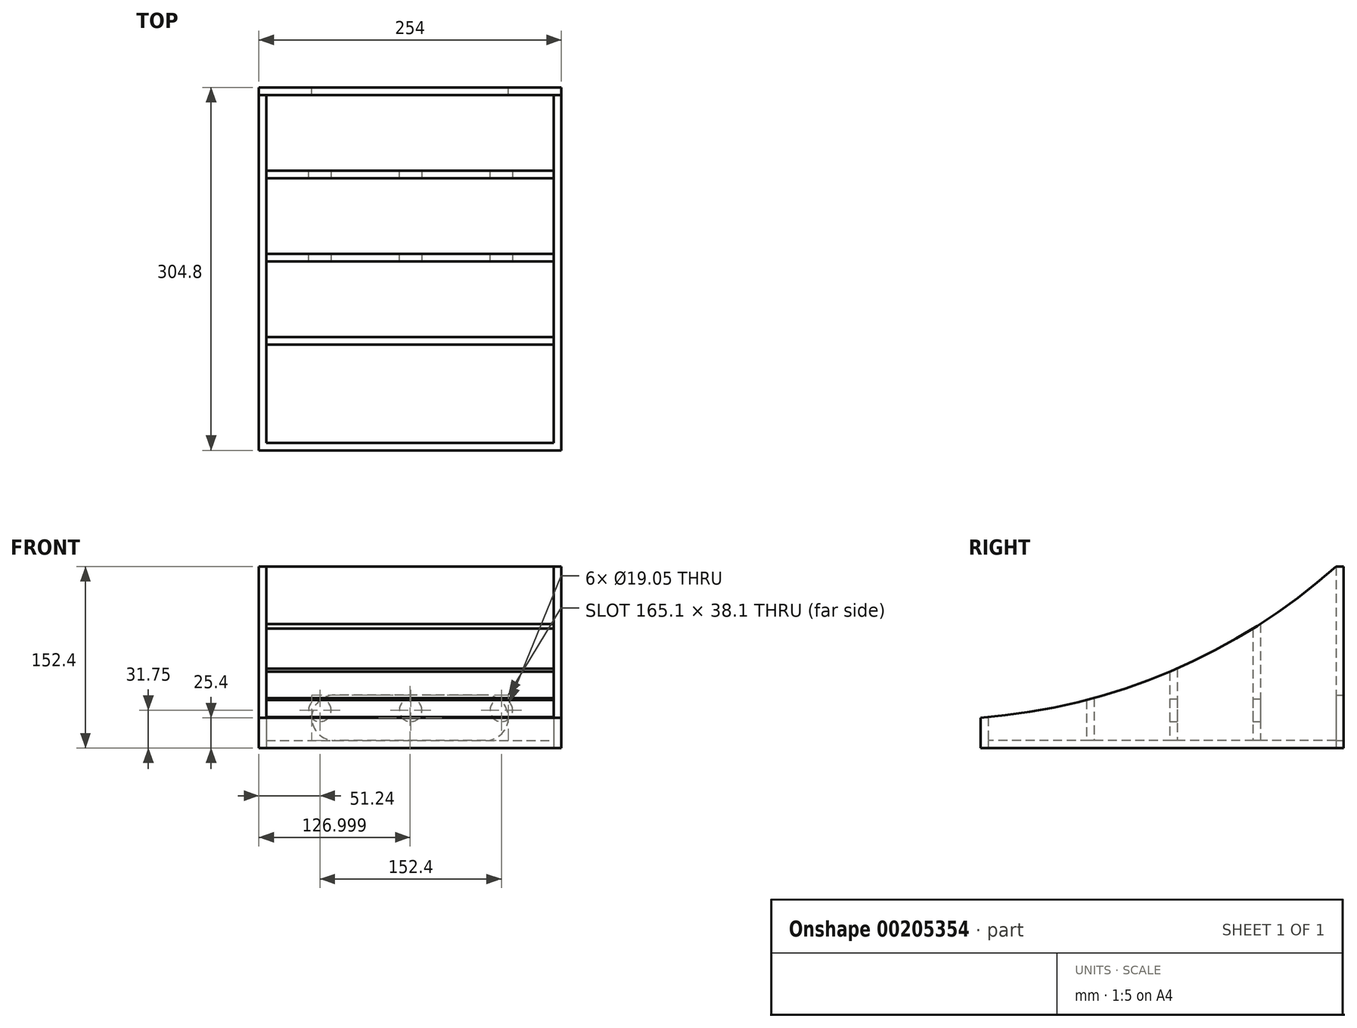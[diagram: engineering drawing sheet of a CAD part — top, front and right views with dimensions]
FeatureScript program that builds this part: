
annotation { "Feature Type Name" : "Feature", "Feature Type Description" : "" }
export const myFeature = defineFeature(function(context is Context, id is Id, definition is map)
    precondition{}
    {
        {
            var Q0;
            Q0=qCreatedBy(makeId("Top.planeOp"),FACE);
            var sketch = newSketch(context, id + "F0", { "sketchPlane" : qUnion([Q0])});
            skLineSegment(sketch, "E0.bottom", {"start": v(-127.44, 180.43) * mm, "end": v(126.56, 180.43) * mm});
            skLineSegment(sketch, "E0.top", {"start": v(-127.44, -124.37) * mm, "end": v(126.56, -124.37) * mm});
            skLineSegment(sketch, "E0.left", {"start": v(-127.44, 180.43) * mm, "end": v(-127.44, -124.37) * mm});
            skLineSegment(sketch, "E0.right", {"start": v(126.56, 180.43) * mm, "end": v(126.56, -124.37) * mm});
            skLineSegment(sketch, "E1.0", {"start": v(-121.1, 174.08) * mm, "end": v(120.2, 174.08) * mm});
            skLineSegment(sketch, "E1.1", {"start": v(-121.1, 174.08) * mm, "end": v(-121.1, -118.02) * mm});
            skLineSegment(sketch, "E1.2", {"start": v(-121.1, -118.02) * mm, "end": v(120.2, -118.02) * mm});
            skLineSegment(sketch, "E1.3", {"start": v(120.2, 174.08) * mm, "end": v(120.2, -118.02) * mm});
            skSolve(sketch);
        }
        {
            var Q0;
            Q0=makeQuery(id+"F0.imprint","IMPRINT",FACE,{"disambiguationData":[TD([[makeQuery(id+"F0.imprint","IMPRINT",EDGE,{"derivedFrom":sQuery(id+"F0.wireOp",EDGE,"E0.bottom")}),-1.0]])]});
            extrude(context, id + "F1", {"entities" : qUnion([Q0]), "depth" : 152.4 * mm});
        }
        {
            var Q0;
            Q0=makeQuery(id+"F1.opExtrude","SWEPT_FACE",FACE,{"disambiguationData":[OSD([sQuery(id+"F0.wireOp",EDGE,"E0.right")])]});
            var sketch = newSketch(context, id + "F2", { "sketchPlane" : qUnion([Q0])});
            skLineSegment(sketch, "E2", {"start": v(-124.37, 25.4) * mm, "end": v(-124.37, 152.4) * mm});
            skLineSegment(sketch, "E3", {"start": v(-124.37, 152.4) * mm, "end": v(174.08, 152.4) * mm});
            skArc(sketch, "E4", {"start": v(-124.37, 25.4) * mm, "mid": v(35.27, 64.44) * mm, "end": v(174.08, 152.4) * mm});
            skSolve(sketch);
        }
        {
            var Q0;
            Q0=makeQuery(id+"F2.imprint","IMPRINT",FACE,{"disambiguationData":[TD([[makeQuery(id+"F2.imprint","IMPRINT",EDGE,{"derivedFrom":sQuery(id+"F2.wireOp",EDGE,"U3Ey406r-KCkc-ZSK3-Qntd-VtqlKmCWQL3E")}),-1.0]])]});
            var Q1;
            Q1=makeQuery(id+"F2.imprint","IMPRINT",FACE,{"disambiguationData":[TD([[makeQuery(id+"F2.imprint","IMPRINT",EDGE,{"derivedFrom":sQuery(id+"F2.wireOp",EDGE,"E2")}),1.0]])]});
            var Q2;
            Q2=makeQuery(id+"F1.opExtrude","SWEPT_FACE",FACE,{"disambiguationData":[OSD([sQuery(id+"F0.wireOp",EDGE,"E0.left")])]});
            extrude(context, id + "F3", {"entities" : qUnion([Q0, Q1]), "operationType" : NewBodyOperationType.REMOVE, "endBound" : BoundingType.UP_TO_SURFACE, "oppositeDirection" : true, "endBoundEntityFace" : qUnion([Q2]), "depth" : 309.88 * mm});
        }
        {
            var Q0;
            Q0=makeQuery(id+"F1.opExtrude","CAP_FACE",FACE,{"disambiguationData":[OSD([sQuery(id+"F0.wireOp",EDGE,"E0.bottom"),sQuery(id+"F0.wireOp",EDGE,"E0.top"),sQuery(id+"F0.wireOp",EDGE,"E0.left"),sQuery(id+"F0.wireOp",EDGE,"E0.right"),sQuery(id+"F0.wireOp",EDGE,"E1.0"),sQuery(id+"F0.wireOp",EDGE,"E1.1"),sQuery(id+"F0.wireOp",EDGE,"E1.2"),sQuery(id+"F0.wireOp",EDGE,"E1.3")])],"isStart":true});
            var sketch = newSketch(context, id + "F4", { "sketchPlane" : qUnion([Q0])});
            skLineSegment(sketch, "E5.bottom", {"start": v(-121.1, -174.08) * mm, "end": v(120.2, -174.08) * mm});
            skLineSegment(sketch, "E5.top", {"start": v(-121.1, 118.02) * mm, "end": v(120.2, 118.02) * mm});
            skLineSegment(sketch, "E5.left", {"start": v(-121.1, -174.08) * mm, "end": v(-121.1, 118.02) * mm});
            skLineSegment(sketch, "E5.right", {"start": v(120.2, -174.08) * mm, "end": v(120.2, 118.02) * mm});
            skSolve(sketch);
        }
        {
            var Q0;
            Q0=makeQuery(id+"F4.imprint","IMPRINT",FACE,{"disambiguationData":[TD([[makeQuery(id+"F4.imprint","IMPRINT",EDGE,{"derivedFrom":sQuery(id+"F4.wireOp",EDGE,"E5.bottom")}),1.0]])]});
            extrude(context, id + "F5", {"entities" : qUnion([Q0]), "oppositeDirection" : true, "depth" : 6.35 * mm});
        }
        {
            var Q0;
            Q0=makeQuery(id+"F5.opExtrude","CAP_FACE",FACE,{"disambiguationData":[OSD([sQuery(id+"F4.wireOp",EDGE,"E5.bottom"),sQuery(id+"F4.wireOp",EDGE,"E5.top"),sQuery(id+"F4.wireOp",EDGE,"E5.left"),sQuery(id+"F4.wireOp",EDGE,"E5.right")])],"isStart":false});
            var sketch = newSketch(context, id + "F6", { "sketchPlane" : qUnion([Q0])});
            skLineSegment(sketch, "E6.bottom", {"start": v(-121.1, 110.58) * mm, "end": v(120.2, 110.58) * mm});
            skLineSegment(sketch, "E6.top", {"start": v(-121.1, 104.23) * mm, "end": v(120.2, 104.23) * mm});
            skLineSegment(sketch, "E6.left", {"start": v(-121.1, 110.58) * mm, "end": v(-121.1, 104.23) * mm});
            skLineSegment(sketch, "E6.right", {"start": v(120.2, 110.58) * mm, "end": v(120.2, 104.23) * mm});
            skLineSegment(sketch, "E7.bottom", {"start": v(-121.1, 40.73) * mm, "end": v(120.2, 40.73) * mm});
            skLineSegment(sketch, "E7.top", {"start": v(-121.1, 34.38) * mm, "end": v(120.2, 34.38) * mm});
            skLineSegment(sketch, "E7.left", {"start": v(-121.1, 40.73) * mm, "end": v(-121.1, 34.38) * mm});
            skLineSegment(sketch, "E7.right", {"start": v(120.2, 40.73) * mm, "end": v(120.2, 34.38) * mm});
            skLineSegment(sketch, "E8.bottom", {"start": v(-121.1, -29.12) * mm, "end": v(120.2, -29.12) * mm});
            skLineSegment(sketch, "E8.top", {"start": v(-121.1, -35.47) * mm, "end": v(120.2, -35.47) * mm});
            skLineSegment(sketch, "E8.left", {"start": v(-121.1, -29.12) * mm, "end": v(-121.1, -35.47) * mm});
            skLineSegment(sketch, "E8.right", {"start": v(120.2, -29.12) * mm, "end": v(120.2, -35.47) * mm});
            skSolve(sketch);
        }
        {
            var Q0;
            Q0=makeQuery(id+"F6.imprint","IMPRINT",FACE,{"disambiguationData":[TD([[makeQuery(id+"F6.imprint","IMPRINT",EDGE,{"derivedFrom":sQuery(id+"F6.wireOp",EDGE,"E7.bottom")}),-1.0]])]});
            var Q1;
            Q1=makeQuery(id+"F6.imprint","IMPRINT",FACE,{"disambiguationData":[TD([[makeQuery(id+"F6.imprint","IMPRINT",EDGE,{"derivedFrom":sQuery(id+"F6.wireOp",EDGE,"E6.bottom")}),-1.0]])]});
            var Q2;
            Q2=makeQuery(id+"F6.imprint","IMPRINT",FACE,{"disambiguationData":[TD([[makeQuery(id+"F6.imprint","IMPRINT",EDGE,{"derivedFrom":sQuery(id+"F6.wireOp",EDGE,"E8.bottom")}),-1.0]])]});
            var Q3;
            Q3=makeQuery(id+"F3.boolean.opBoolean","COPY",FACE,{"derivedFrom":makeQuery(id+"F3.opExtrude","SWEPT_FACE",FACE,{"disambiguationData":[OSD([sQuery(id+"F2.wireOp",EDGE,"E4")])]})});
            extrude(context, id + "F7", {"entities" : qUnion([Q0, Q1, Q2]), "endBound" : BoundingType.UP_TO_SURFACE, "endBoundEntityFace" : qUnion([Q3]), "depth" : 25.4 * mm});
        }
        {
            var Q0;
            Q0=makeQuery(id+"F1.opExtrude","SWEPT_FACE",FACE,{"disambiguationData":[OSD([sQuery(id+"F0.wireOp",EDGE,"E0.bottom")])]});
            var sketch = newSketch(context, id + "F8", { "sketchPlane" : qUnion([Q0])});
            skLineSegment(sketch, "E9.bottom", {"start": v(-63.06, 44.45) * mm, "end": v(63.94, 44.45) * mm});
            skLineSegment(sketch, "E9.top", {"start": v(-63.06, 6.35) * mm, "end": v(63.94, 6.35) * mm});
            skArc(sketch, "E10", {"start": v(-63.06, 44.45) * mm, "mid": v(-82.1, 25.4) * mm, "end": v(-63.06, 6.35) * mm});
            skArc(sketch, "E11", {"start": v(63.94, 6.35) * mm, "mid": v(83, 25.4) * mm, "end": v(63.94, 44.45) * mm});
            skSolve(sketch);
        }
        {
            var Q0;
            Q0=makeQuery(id+"F8.imprint","IMPRINT",FACE,{"disambiguationData":[TD([[makeQuery(id+"F8.imprint","IMPRINT",EDGE,{"derivedFrom":sQuery(id+"F8.wireOp",EDGE,"E9.bottom")}),-1.0]])]});
            extrude(context, id + "F9", {"entities" : qUnion([Q0]), "operationType" : NewBodyOperationType.REMOVE, "oppositeDirection" : true, "depth" : 12.7 * mm});
        }
        {
            var Q0;
            Q0=makeQuery(id+"F7.opExtrude","SWEPT_FACE",FACE,{"disambiguationData":[OSD([sQuery(id+"F6.wireOp",EDGE,"E6.bottom")])]});
            var sketch = newSketch(context, id + "F10", { "sketchPlane" : qUnion([Q0])});
            skCircle(sketch, "E12", {"center": v(-76.2, 31.75) * mm, "radius": 9.53 * mm});
            skCircle(sketch, "E13", {"center": v(0, 31.75) * mm, "radius": 9.53 * mm});
            skCircle(sketch, "E14", {"center": v(76.2, 31.75) * mm, "radius": 9.53 * mm});
            skSolve(sketch);
        }
        {
            var Q0;
            Q0=makeQuery(id+"F10.imprint","IMPRINT",FACE,{"disambiguationData":[TD([[makeQuery(id+"F10.imprint","IMPRINT",EDGE,{"derivedFrom":sQuery(id+"F10.wireOp",EDGE,"E14")}),1.0]])]});
            var Q1;
            Q1=makeQuery(id+"F10.imprint","IMPRINT",FACE,{"disambiguationData":[TD([[makeQuery(id+"F10.imprint","IMPRINT",EDGE,{"derivedFrom":sQuery(id+"F10.wireOp",EDGE,"E13")}),1.0]])]});
            var Q2;
            Q2=makeQuery(id+"F10.imprint","IMPRINT",FACE,{"disambiguationData":[TD([[makeQuery(id+"F10.imprint","IMPRINT",EDGE,{"derivedFrom":sQuery(id+"F10.wireOp",EDGE,"E12")}),1.0]])]});
            extrude(context, id + "F11", {"entities" : qUnion([Q0, Q1, Q2]), "operationType" : NewBodyOperationType.REMOVE, "oppositeDirection" : true, "depth" : 99.06 * mm});
        }
        {
            var Q0;
            Q0=makeQuery(id+"F7.opExtrude","SWEPT_FACE",FACE,{"disambiguationData":[OSD([sQuery(id+"F6.wireOp",EDGE,"E7.bottom")])]});
            var sketch = newSketch(context, id + "F12", { "sketchPlane" : qUnion([Q0])});
            skCircle(sketch, "E15", {"center": v(-76.2, 31.75) * mm, "radius": 9.53 * mm});
            skCircle(sketch, "E16", {"center": v(0, 31.75) * mm, "radius": 9.53 * mm});
            skCircle(sketch, "E17", {"center": v(76.2, 31.75) * mm, "radius": 9.53 * mm});
            skSolve(sketch);
        }
        {
            var Q0;
            Q0=makeQuery(id+"F12.imprint","IMPRINT",FACE,{"disambiguationData":[TD([[makeQuery(id+"F12.imprint","IMPRINT",EDGE,{"derivedFrom":sQuery(id+"F12.wireOp",EDGE,"E16")}),1.0]])]});
            var Q1;
            Q1=makeQuery(id+"F12.imprint","IMPRINT",FACE,{"disambiguationData":[TD([[makeQuery(id+"F12.imprint","IMPRINT",EDGE,{"derivedFrom":sQuery(id+"F12.wireOp",EDGE,"E15")}),1.0]])]});
            var Q2;
            Q2=makeQuery(id+"F12.imprint","IMPRINT",FACE,{"disambiguationData":[TD([[makeQuery(id+"F12.imprint","IMPRINT",EDGE,{"derivedFrom":sQuery(id+"F12.wireOp",EDGE,"E17")}),1.0]])]});
            extrude(context, id + "F13", {"entities" : qUnion([Q0, Q1, Q2]), "operationType" : NewBodyOperationType.REMOVE, "oppositeDirection" : true, "depth" : 25.4 * mm});
        }
    });
